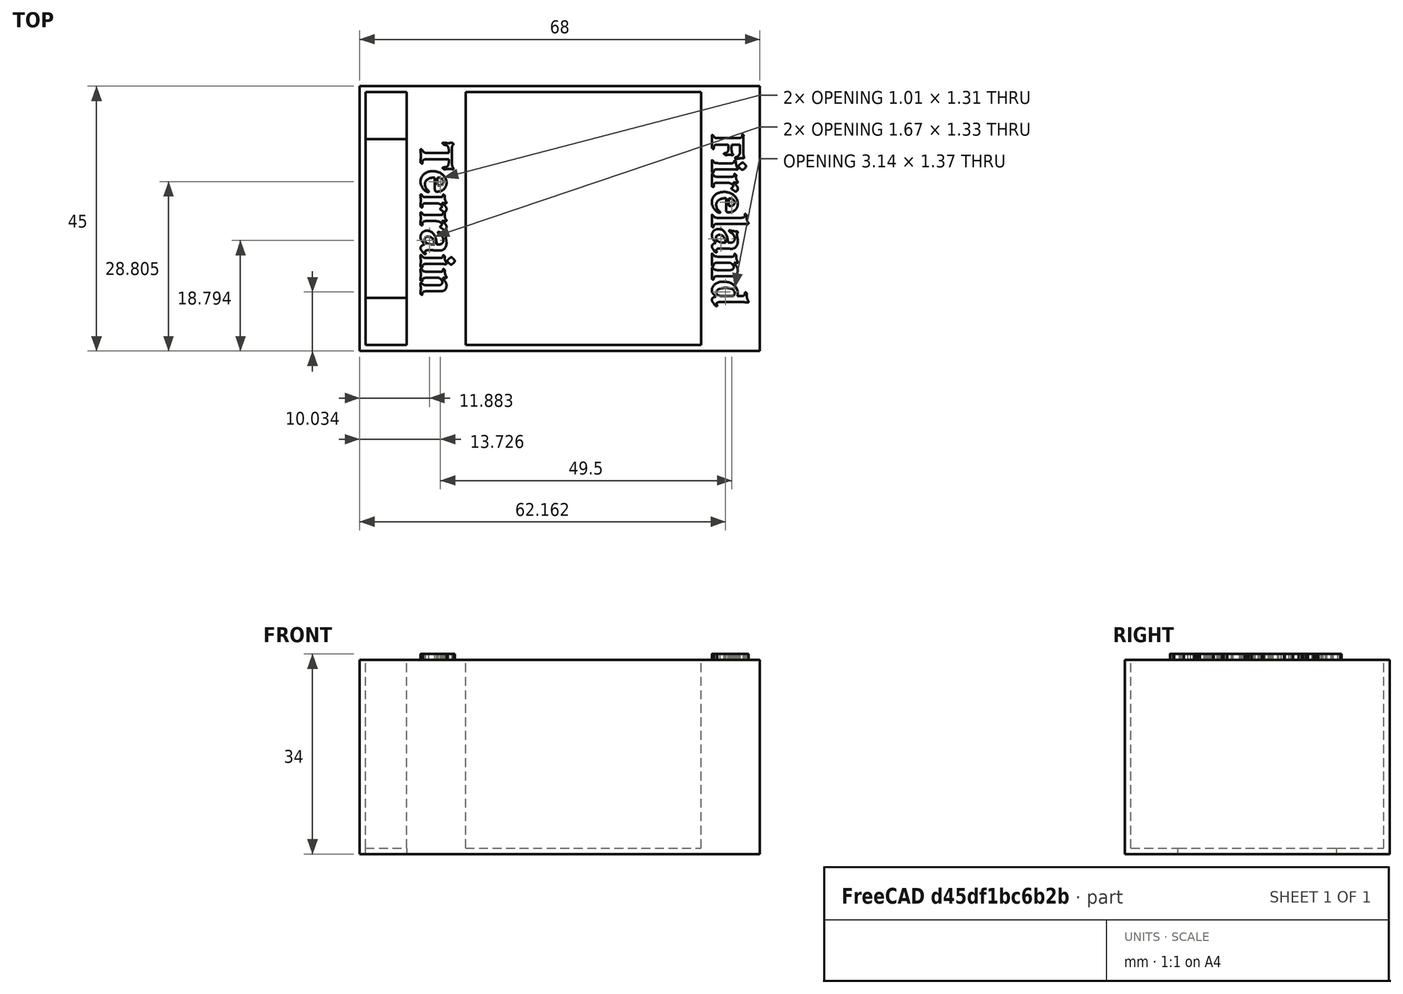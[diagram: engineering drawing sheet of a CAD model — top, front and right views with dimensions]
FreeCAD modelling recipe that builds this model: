
FCSTD DOCUMENT  (FreeCAD 0.18R4 (GitTag))
Label: fireland
License: All rights reserved
LicenseURL: http://en.wikipedia.org/wiki/All_rights_reserved
objects: Part::Box×9, Part::MultiFuse×5, Part::Cut×2, Part::Part2DObjectPython×2, Part::Extrusion×2
note: 20 computed .brp shape members not serialized (recipe doc carries the construction recipe); baked Part::Feature solids carry a one-line shape summary decoded from their .brp

FEATURE [Part::Box] Box  label="Cube"
  AttacherType = Attacher::AttachEngine3D
  Height = 33
  Length = 202
  Placement = pos=(0,-1,0) rot=(0,0,1;0rad)
  Width = 45
FEATURE [Part::Box] Box001  label="Cube001"
  AttacherType = Attacher::AttachEngine3D
  Height = 33
  Length = 200
  Placement = pos=(1,0,0) rot=(0,0,1;0rad)
  Width = 43
FEATURE [Part::Cut] Cut
  Base = -> Box
  Tool = -> Box001
FEATURE [Part::Box] Box002  label="Cube002"
  AttacherType = Attacher::AttachEngine3D
  Height = 1
  Length = 202
  Width = 8
FEATURE [Part::Box] Box003  label="Cube003"
  AttacherType = Attacher::AttachEngine3D
  Height = 1
  Length = 202
  Placement = pos=(0,35,0) rot=(0,0,1;0rad)
  Width = 8
FEATURE [Part::MultiFuse] Fusion
  Shapes = -> [Cut,Box002,Box003]
FEATURE [Part::Box] Box004  label="Cube004"
  AttacherType = Attacher::AttachEngine3D
  Height = 33
  Length = 10
  Placement = pos=(8,0,0) rot=(0,0,1;0rad)
  Width = 43
FEATURE [Part::Box] Box005  label="Cube005"
  AttacherType = Attacher::AttachEngine3D
  Height = 33
  Length = 10
  Placement = pos=(58,0,0) rot=(0,0,1;0rad)
  Width = 43
FEATURE [Part::Box] Box006  label="Cube006"
  AttacherType = Attacher::AttachEngine3D
  Height = 33
  Length = 151
  Placement = pos=(68,-1,0) rot=(0,0,1;0rad)
  Width = 45
FEATURE [Part::MultiFuse] Fusion001
  Shapes = -> [Fusion,Box004,Box005]
FEATURE [Part::Cut] Cut001
  Base = -> Fusion001
  Tool = -> Box006
FEATURE [Part::Box] Box007  label="Cube007"
  AttacherType = Attacher::AttachEngine3D
  Height = 1
  Length = 40
  Placement = pos=(18,0,0) rot=(0,0,1;0rad)
  Width = 43
FEATURE [Part::MultiFuse] Fusion002
  Shapes = -> [Box007,Cut001]
FEATURE [Part::Box] Box008  label="Cube008"
  AttacherType = Attacher::AttachEngine3D
  Height = 33
  Length = 10
  Placement = pos=(58,0,0) rot=(0,0,1;0rad)
  Width = 43
FEATURE [Part::MultiFuse] Fusion003
  Shapes = -> [Fusion002,Box008]
FEATURE [Part::Part2DObjectPython] ShapeString  # Draft 2D object (typed FeaturePython)
  FontFile = <userpath>/Downloads/talisman/Caxton Bold.otf
  Placement = pos=(74,111,0) rot=(0,0,1;0rad)
  Size = 3
  String = Fireland
  Tracking = 0
FEATURE [Part::Part2DObjectPython] ShapeString001  # Draft 2D object (typed FeaturePython)
  FontFile = <userpath>/Downloads/talisman/Caxton Bold.otf
  Placement = pos=(74,111,0) rot=(0,0,1;0rad)
  Size = 3
  String = Terrain
  Tracking = 0
FEATURE [Part::Extrusion] Extrude
  Base = -> ShapeString
  Dir = (0,0,1)
  DirMode = 2
  FaceMakerClass = Part::FaceMakerBullseye
  LengthFwd = 1
  LengthRev = 0
  Placement = pos=(-51,110,33) rot=(0,0,-1;1.5708rad)
  Solid = false
  Symmetric = false
FEATURE [Part::Extrusion] Extrude001
  Base = -> ShapeString001
  Dir = (0,0,1)
  DirMode = 2
  FaceMakerClass = Part::FaceMakerBullseye
  LengthFwd = 1
  LengthRev = 0
  Placement = pos=(-100.5,108.5,33) rot=(0,0,-1;1.5708rad)
  Solid = false
  Symmetric = false
FEATURE [Part::MultiFuse] Fusion004
  Shapes = -> [Extrude,Extrude001]
